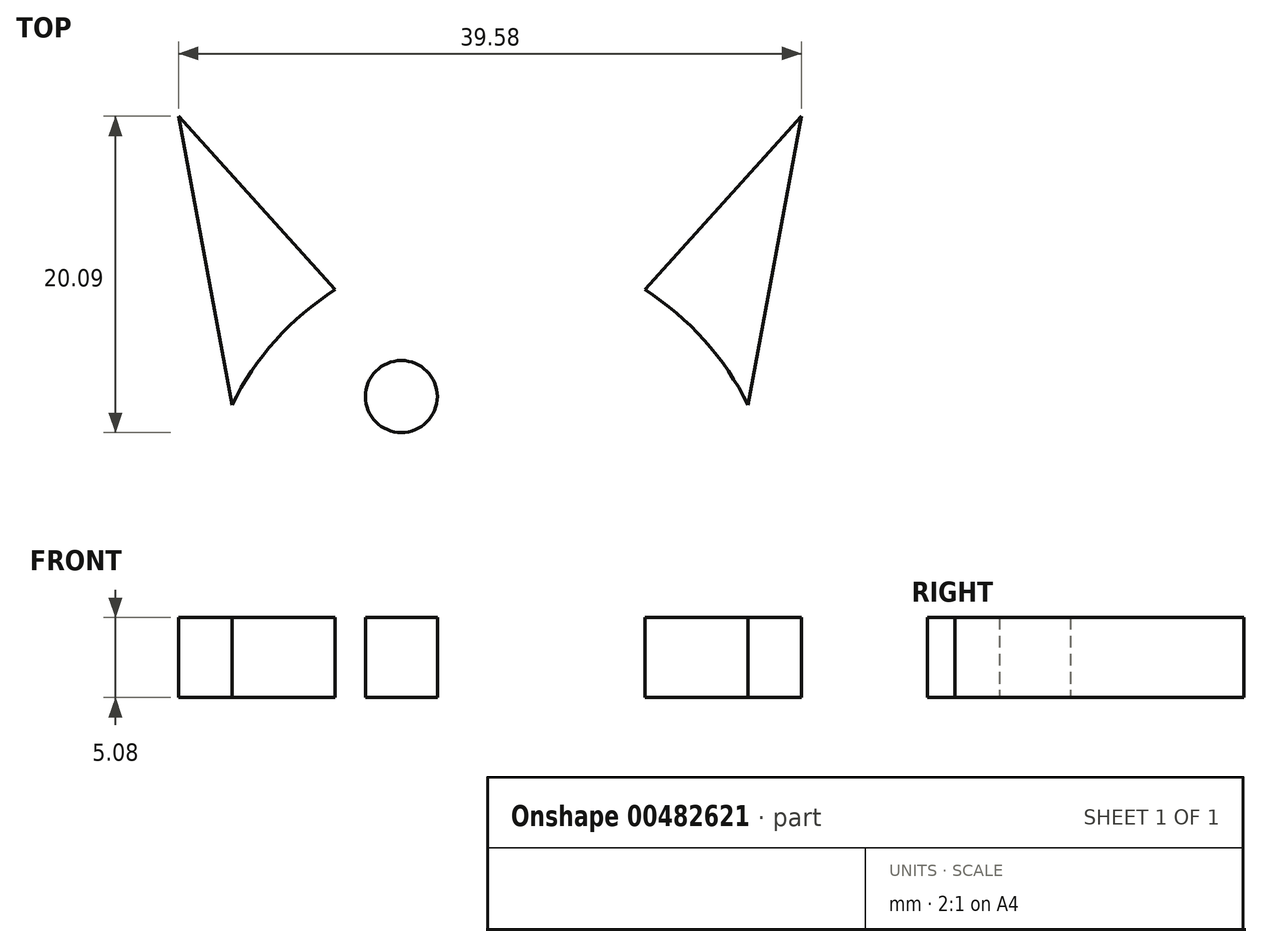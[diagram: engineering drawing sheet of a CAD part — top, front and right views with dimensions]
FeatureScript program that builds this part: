
annotation { "Feature Type Name" : "Feature", "Feature Type Description" : "" }
export const myFeature = defineFeature(function(context is Context, id is Id, definition is map)
    precondition{}
    {
        {
            var Q0;
            Q0=qCreatedBy(makeId("Top.planeOp"),FACE);
            var sketch = newSketch(context, id + "F0", { "sketchPlane" : qUnion([Q0])});
            skCircle(sketch, "E0", {"center": v(0, 0) * mm, "radius": 18.28 * mm});
            skPoint(sketch, "E1.MirrorP", {"position": v(-9.81, 15.4) * mm});
            skPoint(sketch, "E2.MirrorP", {"position": v(-16.4, 8.09) * mm});
            skPoint(sketch, "E3.MirrorP", {"position": v(9.81, 15.4) * mm});
            skLineSegment(sketch, "E4.MirrorCS", {"start": v(-19.8, 26.43) * mm, "end": v(-9.81, 15.4) * mm});
            skPoint(sketch, "E5.MirrorP", {"position": v(16.4, 8.09) * mm});
            skPoint(sketch, "E6.MirrorP", {"position": v(-19.8, 26.43) * mm});
            skLineSegment(sketch, "E7.MirrorCS", {"start": v(9.81, 15.4) * mm, "end": v(19.8, 26.43) * mm});
            skCircle(sketch, "E8.MirrorC", {"center": v(-5.63, 8.63) * mm, "radius": 2.29 * mm});
            skLineSegment(sketch, "E9.MirrorCS", {"start": v(-19.8, 26.43) * mm, "end": v(-16.4, 8.09) * mm});
            skLineSegment(sketch, "E10.MirrorCS", {"start": v(16.4, 8.09) * mm, "end": v(19.8, 26.43) * mm});
            skPoint(sketch, "E11.MirrorP", {"position": v(19.8, 26.43) * mm});
            skCircle(sketch, "E12.MirrorC", {"center": v(5.63, 8.63) * mm, "radius": 2.29 * mm});
            skArc(sketch, "E13", {"start": v(-11.17, -3.07) * mm, "mid": v(-6.15, -5.26) * mm, "end": v(-0.76, -6.27) * mm});
            skLineSegment(sketch, "E14", {"start": v(-0.76, 0) * mm, "end": v(-0.76, -6.27) * mm});
            skLineSegment(sketch, "E15.MirrorCS", {"start": v(0.76, 0) * mm, "end": v(0.76, -6.27) * mm});
            skArc(sketch, "E16.MirrorCS", {"start": v(11.17, -3.07) * mm, "mid": v(6.15, -5.26) * mm, "end": v(0.76, -6.27) * mm});
            skLineSegment(sketch, "E17", {"start": v(-0.76, 0) * mm, "end": v(0.76, 0) * mm});
            skPoint(sketch, "E18", {"position": v(-0.76, 0) * mm});
            skPoint(sketch, "E19", {"position": v(-0.76, -6.27) * mm});
            skPoint(sketch, "E20", {"position": v(0.76, 0) * mm});
            skPoint(sketch, "E21", {"position": v(11.17, -3.07) * mm});
            skArc(sketch, "E22", {"start": v(-11.17, -3.07) * mm, "mid": v(0, -8.3) * mm, "end": v(11.17, -3.07) * mm});
            skPoint(sketch, "E23", {"position": v(-2.77, 2.3) * mm});
            skPoint(sketch, "E24", {"position": v(2.77, 2.3) * mm});
            skLineSegment(sketch, "E25", {"start": v(-2.77, 2.3) * mm, "end": v(2.77, 2.3) * mm});
            skPoint(sketch, "E26", {"position": v(0, 2.3) * mm});
            skLineSegment(sketch, "E27", {"start": v(-2.77, 2.3) * mm, "end": v(-0.76, 0) * mm});
            skLineSegment(sketch, "E28", {"start": v(0.76, 0) * mm, "end": v(2.77, 2.3) * mm});
            skSolve(sketch);
        }
        {
            var Q0;
            Q0=makeQuery(id+"F0.imprint","IMPRINT",FACE,{"disambiguationData":[TD([[makeQuery(id+"F0.imprint","IMPRINT",EDGE,{"derivedFrom":sQuery(id+"F0.wireOp",EDGE,"E8.MirrorC")}),1.0]])]});
            var Q1;
            {var subQ0=sQuery(id+"F0.wireOp",EDGE,"E10.MirrorCS");Q1=makeQuery(id+"F0.imprint","IMPRINT",FACE,{"disambiguationData":[TD([[makeQuery(id+"F0.imprint","IMPRINT",EDGE,{"derivedFrom":subQ0}),1.0]])]});}
            var Q2;
            {var subQ0=sQuery(id+"F0.wireOp",EDGE,"E9.MirrorCS");Q2=makeQuery(id+"F0.imprint","IMPRINT",FACE,{"disambiguationData":[TD([[makeQuery(id+"F0.imprint","IMPRINT",EDGE,{"derivedFrom":subQ0}),1.0]])]});}
            extrude(context, id + "F1", {"entities" : qUnion([Q0, Q1, Q2]), "depth" : 5.08 * mm});
        }
    });
